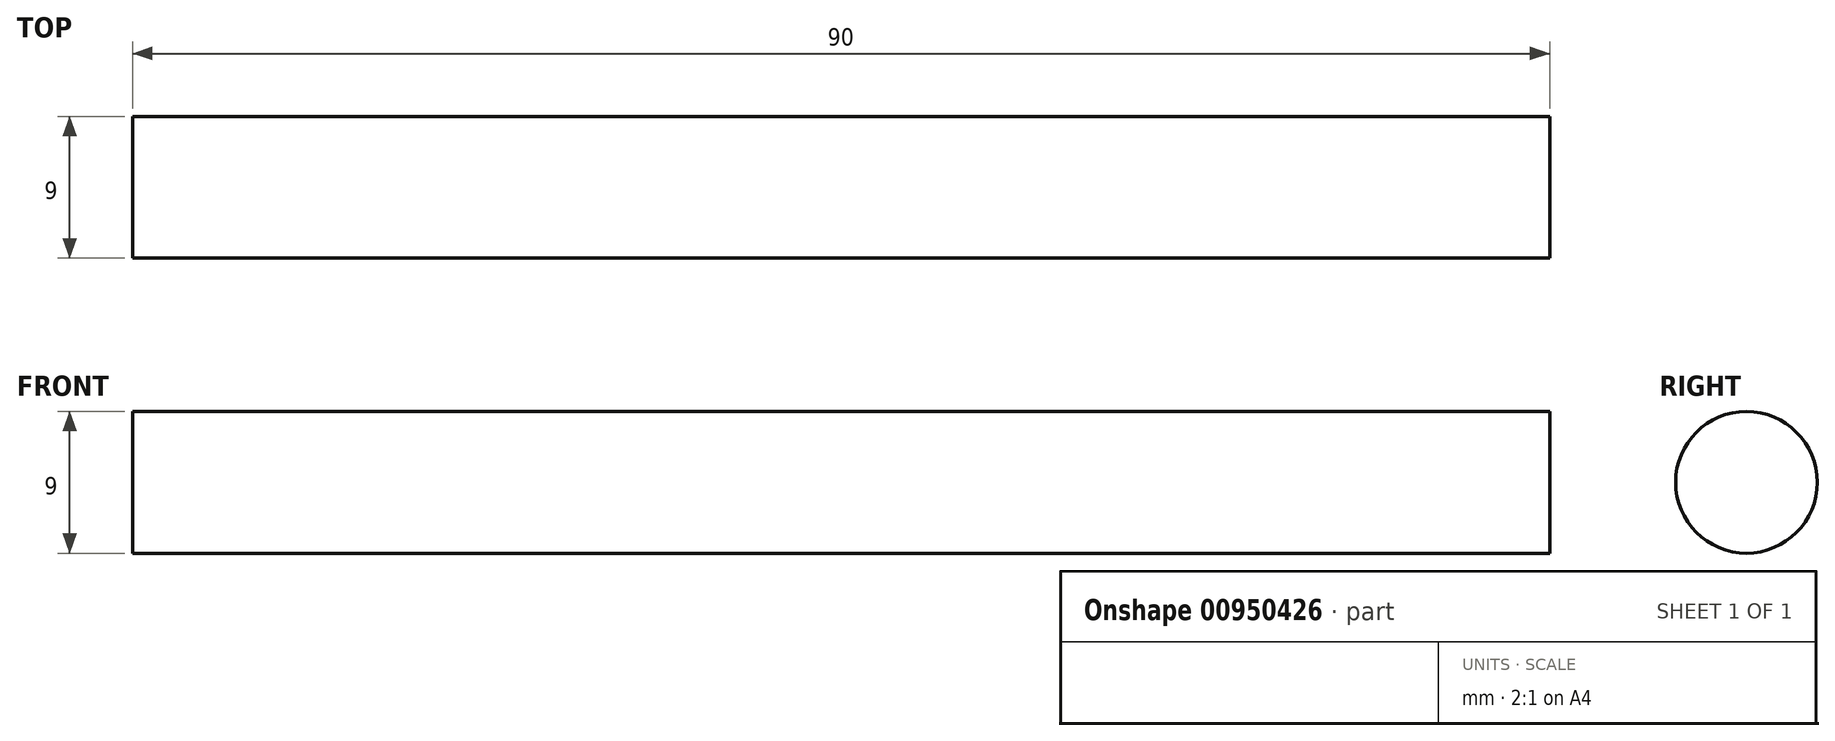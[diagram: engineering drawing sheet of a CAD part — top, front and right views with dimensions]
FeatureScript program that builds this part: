
annotation { "Feature Type Name" : "Feature", "Feature Type Description" : "" }
export const myFeature = defineFeature(function(context is Context, id is Id, definition is map)
    precondition{}
    {
        {
            var Q0;
            Q0=qCreatedBy(makeId("Right.planeOp"), FACE);
            var sketch = newSketch(context, id + "F0", { "sketchPlane" : qUnion([Q0])});
            skCircle(sketch, "E0", {"center": v(0, 0) * mm, "radius": 4.5 * mm});
            skSolve(sketch);
        }
        {
            var Q0;
            Q0 = qSketchRegion(id + "F0", true);
            extrude(context, id + "F1", {"entities" : qUnion([Q0]), "domain" : OperationDomain.MODEL, "flatOperationType" : FlatOperationType.REMOVE, "depth" : 90 * mm, "offsetDistance" : 25 * mm});
        }
    });
